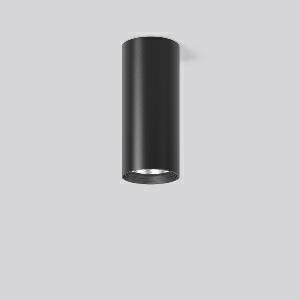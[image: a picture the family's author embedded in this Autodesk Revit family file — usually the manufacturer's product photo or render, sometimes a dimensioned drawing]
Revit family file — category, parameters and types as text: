
# Revit family: heledon_mini_a_931201_003_1_76_9f3e
name_source: partatom
category: Lighting Fixtures
units: mm (PartAtom-declared; Revit-internal decimal feet)

## family parameters
Cut with Voids When Loaded = No
Host = Face
Light Source = No
Part Type = Normal
Room Calculation Point = No
Round Connector Dimension = Use Diameter
Shared = No

## types (1)
- HELEDON mini A (1 x LED Modul 940, 2600 lm, 4000)
    Apparent Load = 20 VA
    Approval mark = CE
    CIE Flux Codes = 99 100 100 100 100
    Color Rendering = 92
    Color Temperature = 4000
    Default Elevation = 1800 mm
    Description = Series: HELEDON mini
Cylindrical surface-mounted downlight. Housing: die-cast aluminium, powder-coated. Internal ceiling frame polycarbonate with bayonet mounting. Black plastic ring and recessed LED to prevent glare from the side. Optical assembly with reflector made of MIRO-Silver with 98% total light reflection for outstanding efficiency - can be changed without tools. Best colour rendering index Ra>90. Suitable for Ceiling mounting. Easy installation with a separate ceiling frame with bayonet mounting and plug connection. Driver integrated. Connected via plug-in connector. High quality converter without flickering and stroboscopic effect. The following accessories can be mounted without use of tools: interchangeable lenses, decorative glasses, honeycomb louvre, clear and frosted diffusers, white interchangeable plastic ring. 
Colour: deep black, matt (RAL 9005)
Diameter: 87 mm
Height: 197 mm
Lamp: LED
Socket: without socket
Colour temperature: 4000K
Colour rendering index (CRI): 92
System power: 20 W
Rated luminous flux: 2600 lm
Luminous efficiency: 130 lm/W
Control gear: Converter, dimmable, DALI
Protection class: I
Type of protection: IP 20
    Height = 197 mm
    Lamp = 1 x LED Modul 940
    Lamp Light Flux = 2600 lm
    Lamp count = 1
    Length = 87 mm
    Lifetime = 50000 h
    Luminous efficacy = 130 lm/W
    Manufacturer = RZB
    ModVariant = No
    Model = 931201.003.1.76
    Mounting Place = Ceiling
    Mounting Type = Surface mounted
    Number of Poles = 1
    OnlyDefault = Yes
    Power Factor = 1
    Product Name = HELEDON mini A
    Product group = Surface mounted downlights
    ProductGroupID = 302
    Protection Class = Protection class I
    Protection Degree = IP 20
    RLX_Detail_Level = 1
    RLX_Emergency_Light_Flux = 0 lm
    RLX_Emergency_Type = 0
    RLX_Emergency_Type_DB = No
    RlxData = <blob elided: 106289 chars, md5=92820fa7>
    Socket = socket
    Standby Power = 0 W
    System Light Flux = 2600 lm
    System Power = 20 W
    Type Comments = Product without accessories
    Type Image = 931188.003.jpg
    URL = http://relux.com
    VarID = ---
    Voltage = 230 V
    Voltage Range = 220-240 V
    Weight = 0.00 kg
    Width = 0 mm  [stored 0 ft]

note: [stored X ft] marks values corroborated as IEEE doubles in the binary element streams (Revit-internal decimal feet)

## geometry (parser evidence)
native form markers: Blend x4, Sweep x10
no freeform markers — native parametric forms only
